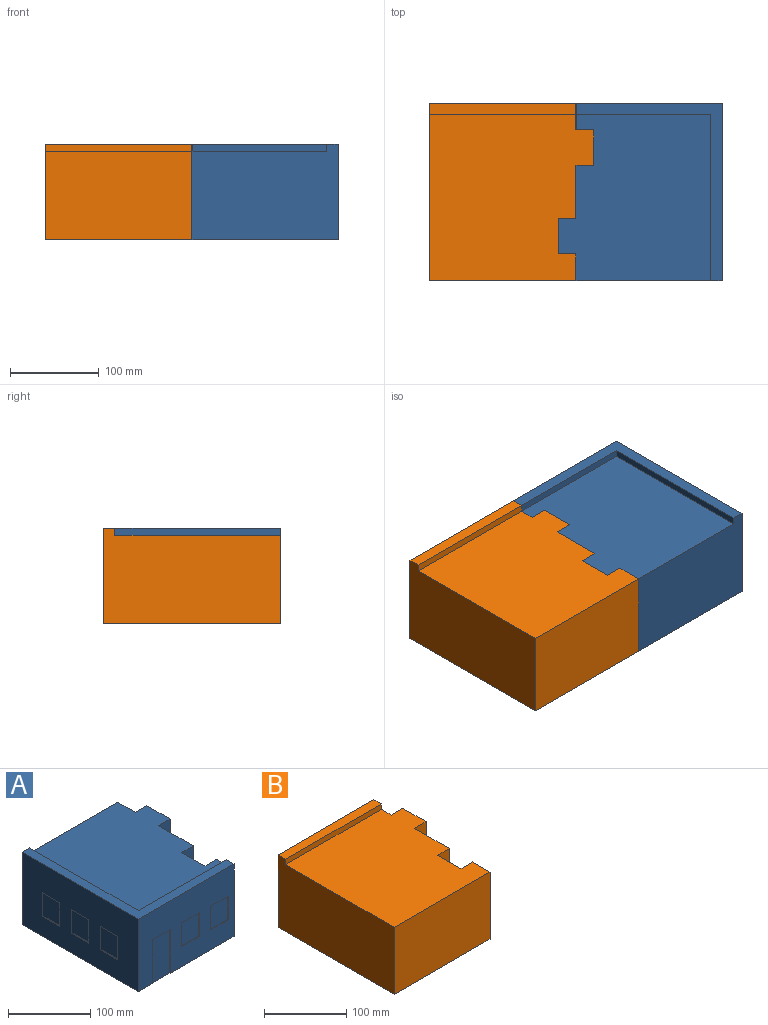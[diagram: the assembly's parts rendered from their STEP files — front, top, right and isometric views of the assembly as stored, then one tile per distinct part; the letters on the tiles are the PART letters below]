
ASSEMBLY  parts=2 mates=1
PART A: 59 faces, bbox 185x200x108 mm
  f0: plane 200x108mm, normal (-1,0,0), area 18450mm2, adj f14,f15,f25,f29,f44,f45,f46,f47
  f1: plane 97.5x20mm, normal (0,1,0), area 1950mm2, adj f2,f12,f25,f26
  f2: plane 97.5x60mm, normal (-1,0,0), area 5850mm2, adj f1,f3,f25,f26
  f3: plane 97.5x20mm, normal (0,1,0), area 1950mm2, adj f2,f4,f25,f26
  f4: plane 97.5x45mm, normal (-1,0,0), area 4387.5mm2, adj f3,f5,f25,f26
  f5: plane 97.5x20mm, normal (0,-1,0), area 1950mm2, adj f4,f6,f25,f26
  f6: plane 97.5x25mm, normal (-1,0,0), area 2437.5mm2, adj f5,f7,f25,f26
  f7: plane 160x97.5mm, normal (0,1,0), area 15600mm2, adj f6,f8,f25,f26
  f8: plane 195x97.5mm, normal (1,0,0), area 19012.5mm2, adj f7,f9,f25,f26
  f9: plane 160x97.5mm, normal (0,-1,0), area 15600mm2, adj f8,f10,f25,f26
  f10: plane 97.5x30mm, normal (-1,0,0), area 2925mm2, adj f9,f11,f25,f26
  f11: plane 97.5x20mm, normal (0,-1,0), area 1950mm2, adj f10,f12,f25,f26
  f12: plane 97.5x35mm, normal (-1,0,0), area 3412.5mm2, adj f1,f11,f25,f26
  f13: plane 100x30mm, normal (1,0,0), area 3000mm2, adj f14,f23,f24,f25
  f14: plane 165x108mm, normal (0,1,0), area 16604mm2, adj f0,f13,f24,f25,f28,f29
  f15: plane 165x108mm, normal (0,-1,0), area 13770mm2, adj f0,f16,f25,f29,f30,f31,f32,f34
  f16: plane 108x30mm, normal (1,0,0), area 3104mm2, adj f15,f17,f24,f25,f27,f29
  f17: plane 100x20mm, normal (0,1,0), area 2000mm2, adj f16,f18,f24,f25
  f18: plane 100x40mm, normal (1,0,0), area 4000mm2, adj f17,f19,f24,f25
  f19: plane 100x20mm, normal (0,-1,0), area 2000mm2, adj f18,f20,f24,f25
  f20: plane 100x60mm, normal (1,0,0), area 6000mm2, adj f19,f21,f24,f25
  f21: plane 100x20mm, normal (0,-1,0), area 2000mm2, adj f20,f22,f24,f25
  f22: plane 100x40mm, normal (1,0,0), area 4000mm2, adj f21,f23,f24,f25
  f23: plane 100x20mm, normal (0,1,0), area 2000mm2, adj f13,f22,f24,f25
  f24: plane 187x172mm, normal (0,0,1), area 28424mm2, adj f13,f14,f16,f17,f18,f19,f20,f21
  f25: plane 200x185mm, normal (0,0,-1), area 1970mm2, adj f0,f1,f2,f3,f4,f5,f6,f7
  f26: plane 195x180mm, normal (0,0,-1), area 31000mm2, adj f1,f2,f3,f4,f5,f6,f7,f8
  f27: plane 152x8mm, normal (0,1,0), area 1216mm2, adj f16,f24,f28,f29
  f28: plane 187x8mm, normal (1,0,0), area 1496mm2, adj f14,f24,f27,f29
  f29: plane 200x165mm, normal (0,0,1), area 4576mm2, adj f0,f14,f15,f16,f27,f28
  f30: plane 65x1mm, normal (-1,0,0), area 65mm2, adj f15,f25,f31,f33
  f31: plane 30x1mm, normal (0,0,-1), area 30mm2, adj f15,f30,f32,f33
  f32: plane 65x1mm, normal (1,0,0), area 65mm2, adj f15,f25,f31,f33
  f33: plane 65x30mm, normal (0,-1,0), area 1950mm2, adj f25,f30,f31,f32
  f34: plane 35x1mm, normal (-1,0,0), area 35mm2, adj f15,f35,f37,f38
  f35: plane 30x1mm, normal (0,0,-1), area 30mm2, adj f15,f34,f36,f38
  f36: plane 35x1mm, normal (1,0,0), area 35mm2, adj f15,f35,f37,f38
  f37: plane 30x1mm, normal (0,0,1), area 30mm2, adj f15,f34,f36,f38
  f38: plane 35x30mm, normal (0,-1,0), area 1050mm2, adj f34,f35,f36,f37
  f39: plane 35x1mm, normal (-1,0,0), area 35mm2, adj f15,f40,f42,f43
  f40: plane 30x1mm, normal (0,0,-1), area 30mm2, adj f15,f39,f41,f43
  f41: plane 35x1mm, normal (1,0,0), area 35mm2, adj f15,f40,f42,f43
  f42: plane 30x1mm, normal (0,0,1), area 30mm2, adj f15,f39,f41,f43
  f43: plane 35x30mm, normal (0,-1,0), area 1050mm2, adj f39,f40,f41,f42
  f44: plane 35x1mm, normal (0,-1,0), area 35mm2, adj f0,f45,f47,f48
  f45: plane 30x1mm, normal (0,0,1), area 30mm2, adj f0,f44,f46,f48
  f46: plane 35x1mm, normal (0,1,0), area 35mm2, adj f0,f45,f47,f48
  f47: plane 30x1mm, normal (0,0,-1), area 30mm2, adj f0,f44,f46,f48
  f48: plane 35x30mm, normal (-1,0,0), area 1050mm2, adj f44,f45,f46,f47
  f49: plane 35x1mm, normal (0,1,0), area 35mm2, adj f0,f50,f52,f53
  f50: plane 30x1mm, normal (0,0,-1), area 30mm2, adj f0,f49,f51,f53
  f51: plane 35x1mm, normal (0,-1,0), area 35mm2, adj f0,f50,f52,f53
  f52: plane 30x1mm, normal (0,0,1), area 30mm2, adj f0,f49,f51,f53
  f53: plane 35x30mm, normal (-1,0,0), area 1050mm2, adj f49,f50,f51,f52
  f54: plane 30x1mm, normal (0,0,-1), area 30mm2, adj f0,f55,f57,f58
  f55: plane 35x1mm, normal (0,-1,0), area 35mm2, adj f0,f54,f56,f58
  f56: plane 30x1mm, normal (0,0,1), area 30mm2, adj f0,f55,f57,f58
  f57: plane 35x1mm, normal (0,1,0), area 35mm2, adj f0,f54,f56,f58
  f58: plane 35x30mm, normal (-1,0,0), area 1050mm2, adj f54,f55,f56,f57
PART B: 44 faces, bbox 185x200x108 mm
  f0: plane 165x108mm, normal (0,1,0), area 14670mm2, adj f1,f2,f13,f15,f29,f30,f31,f32
  f1: plane 108x30mm, normal (1,0,0), area 3104mm2, adj f0,f11,f12,f13,f14,f15
  f2: plane 200x108mm, normal (-1,0,0), area 20104mm2, adj f0,f3,f12,f13,f14,f15
  f3: plane 165x100mm, normal (0,-1,0), area 16500mm2, adj f2,f4,f12,f13
  f4: plane 100x30mm, normal (1,0,0), area 3000mm2, adj f3,f5,f12,f13
  f5: plane 100x20mm, normal (0,1,0), area 2000mm2, adj f4,f6,f12,f13
  f6: plane 100x40mm, normal (1,0,0), area 4000mm2, adj f5,f7,f12,f13
  f7: plane 100x20mm, normal (0,-1,0), area 2000mm2, adj f6,f8,f12,f13
  f8: plane 100x60mm, normal (1,0,0), area 6000mm2, adj f7,f9,f12,f13
  f9: plane 100x20mm, normal (0,-1,0), area 2000mm2, adj f8,f10,f12,f13
  f10: plane 100x40mm, normal (1,0,0), area 4000mm2, adj f9,f11,f12,f13
  f11: plane 100x20mm, normal (0,1,0), area 2000mm2, adj f1,f10,f12,f13
  f12: plane 187x185mm, normal (0,0,1), area 30855mm2, adj f1,f2,f3,f4,f5,f6,f7,f8
  f13: plane 200x185mm, normal (0,0,-1), area 2394mm2, adj f0,f1,f2,f3,f4,f5,f6,f7
  f14: plane 165x8mm, normal (0,-1,0), area 1320mm2, adj f1,f2,f12,f15
  f15: plane 165x13mm, normal (0,0,1), area 2145mm2, adj f0,f1,f2,f14
  f16: plane 97x20mm, normal (0,1,0), area 1940mm2, adj f13,f17,f27,f28
  f17: plane 97x60mm, normal (-1,0,0), area 5820mm2, adj f13,f16,f18,f28
  f18: plane 97x20mm, normal (0,1,0), area 1940mm2, adj f13,f17,f19,f28
  f19: plane 97x34mm, normal (-1,0,0), area 3298mm2, adj f13,f18,f20,f28
  f20: plane 97x20mm, normal (0,-1,0), area 1940mm2, adj f13,f19,f21,f28
  f21: plane 97x30mm, normal (-1,0,0), area 2910mm2, adj f13,f20,f22,f28
  f22: plane 159x97mm, normal (0,-1,0), area 15423mm2, adj f13,f21,f23,f28
  f23: plane 194x97mm, normal (1,0,0), area 18818mm2, adj f13,f22,f24,f28
  f24: plane 159x97mm, normal (0,1,0), area 15423mm2, adj f13,f23,f25,f28
  f25: plane 97x24mm, normal (-1,0,0), area 2328mm2, adj f13,f24,f26,f28
  f26: plane 97x20mm, normal (0,-1,0), area 1940mm2, adj f13,f25,f27,f28
  f27: plane 97x46mm, normal (-1,0,0), area 4462mm2, adj f13,f16,f26,f28
  f28: plane 194x179mm, normal (0,0,-1), area 30606mm2, adj f16,f17,f18,f19,f20,f21,f22,f23
  f29: plane 35x2mm, normal (-1,0,0), area 70mm2, adj f0,f30,f32,f33
  f30: plane 30x2mm, normal (0,0,1), area 60mm2, adj f0,f29,f31,f33
  f31: plane 35x2mm, normal (1,0,0), area 70mm2, adj f0,f30,f32,f33
  f32: plane 30x2mm, normal (0,0,-1), area 60mm2, adj f0,f29,f31,f33
  f33: plane 35x30mm, normal (0,1,0), area 1050mm2, adj f29,f30,f31,f32
  f34: plane 30x2mm, normal (0,0,-1), area 60mm2, adj f0,f35,f37,f38
  f35: plane 35x2mm, normal (-1,0,0), area 70mm2, adj f0,f34,f36,f38
  f36: plane 30x2mm, normal (0,0,1), area 60mm2, adj f0,f35,f37,f38
  f37: plane 35x2mm, normal (1,0,0), area 70mm2, adj f0,f34,f36,f38
  f38: plane 35x30mm, normal (0,1,0), area 1050mm2, adj f34,f35,f36,f37
  f39: plane 35x2mm, normal (-1,0,0), area 70mm2, adj f0,f40,f42,f43
  f40: plane 30x2mm, normal (0,0,1), area 60mm2, adj f0,f39,f41,f43
  f41: plane 35x2mm, normal (1,0,0), area 70mm2, adj f0,f40,f42,f43
  f42: plane 30x2mm, normal (0,0,-1), area 60mm2, adj f0,f39,f41,f43
  f43: plane 35x30mm, normal (0,1,0), area 1050mm2, adj f39,f40,f41,f42
PLACE A rot(axis=(0,0,1),180deg) t=(131.61,61.84,-12.43)mm
PLACE B t=(131.61,61.84,-12.43)mm
MATE fastened A.f22 <-> B.f6  axis (-1,0,0) through (111.61,11.84,37.57)mm
